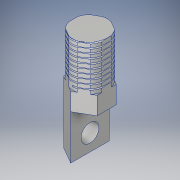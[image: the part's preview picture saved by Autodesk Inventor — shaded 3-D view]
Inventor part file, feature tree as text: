
AUTODESK INVENTOR PART (.ipt)
format: ipt  version: 2018 (Build 220112000, 112)  size: 559,104 bytes
history: native  units: in
note: dims shown in document units (in); Inventor stores cm internally (conversion verified against a paired STEP export)
features: sketch x5, extrude x3, hole x1, helix x1
ambient origin geometry x8: Origin, YZ Plane, XZ Plane, XY Plane, X Axis, Y Axis, Z Axis, Center Point
bodies: Solid1 (feature_tree)
feature tree (10):
  extrude  "Extrusion1"  TaperAngle=90.0deg  [1 undecoded]
  extrude  "Extrusion2"  Depth=1.2in TaperAngle=0.0deg
  hole  "Hole2"  [1 undecoded]
  extrude  "Extrusion3"  Depth=0.05in
  helix  "Coil1"  [1 undecoded]
  sketch  "Sketch1"  dims[d0=0.1875in d1=90.0deg]
  sketch  "Sketch3"  dims[d2=2.3622in d4=360.0deg d6=1.2in d7=0.0in]
  sketch  "Sketch5"  dims[d15=0.5in d16=0.0in d17=0.1875in]
  sketch  "Sketch8"  dims[d18=0.266in]
  sketch  "Sketch9"  dims[d19=0.201in d20=0.5in d21=0.507in d22=0.25in d23=0.5635in d24=1.0in d25=0.8108in d28=0.39in d29=0.5in d30=0.0in d31=0.72in d32=0.04in d33=30.0deg d34=0.04in d35=60.0deg d36=0.05in d37=1.0in d38=3.937in d39=0.0in d40=90.0deg d41=90.0deg d42=0.0in d43=0.0in]
note: 3 required parameter values undecoded (feature->parameter linkage not recoverable at this tier; creation-order binding heuristic only, values carry confidence <= 0.55)
